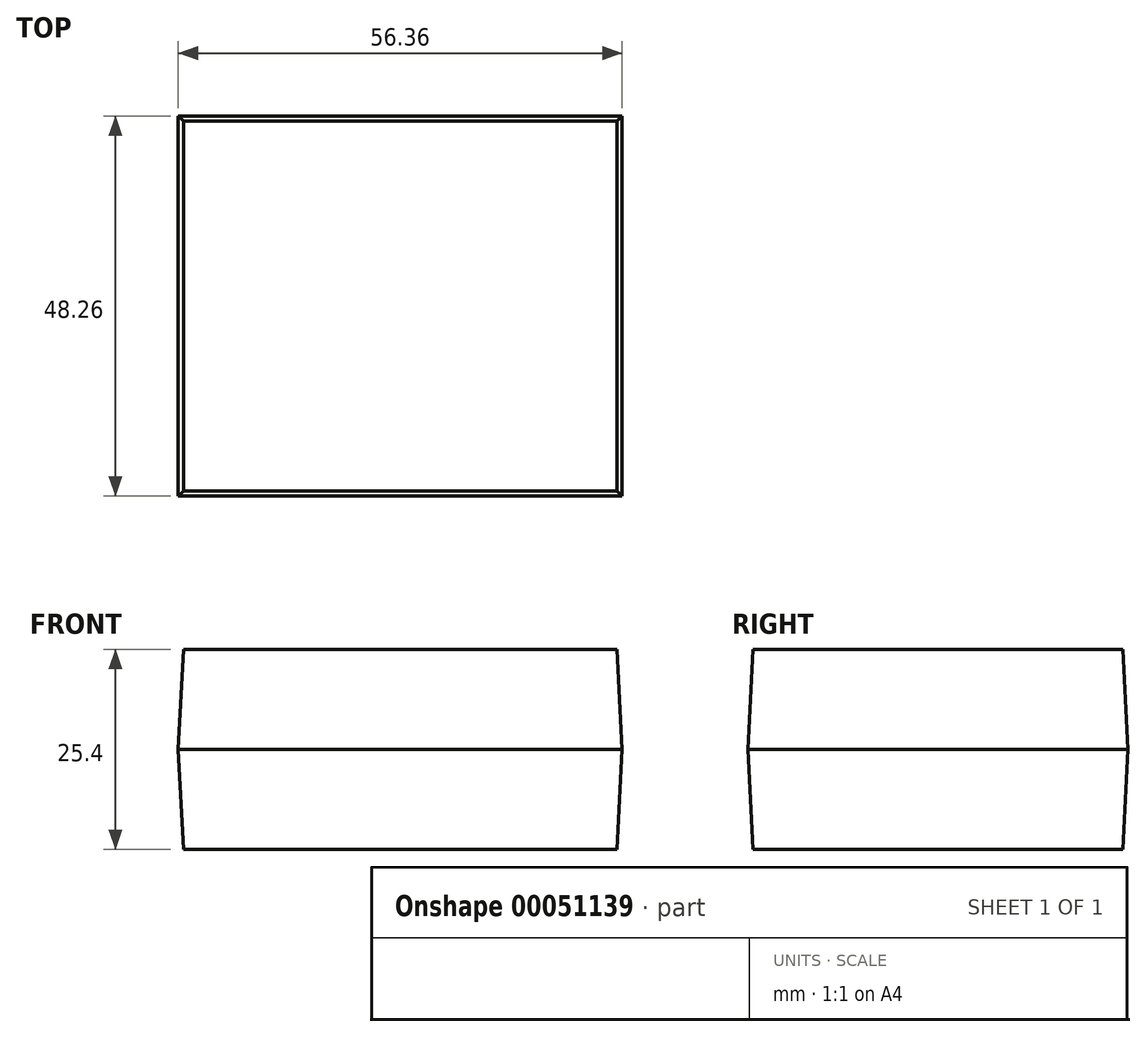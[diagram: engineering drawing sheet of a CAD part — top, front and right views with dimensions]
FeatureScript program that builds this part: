
annotation { "Feature Type Name" : "Feature", "Feature Type Description" : "" }
export const myFeature = defineFeature(function(context is Context, id is Id, definition is map)
    precondition{}
    {
        {
            var Q0;
            Q0=qCreatedBy(makeId("Top.planeOp"),FACE);
            var sketch = newSketch(context, id + "F0", { "sketchPlane" : qUnion([Q0])});
            skLineSegment(sketch, "E0.rect.bottom", {"start": v(28.18, -24.13) * mm, "end": v(-28.18, -24.13) * mm});
            skLineSegment(sketch, "E0.rect.top", {"start": v(28.18, 24.13) * mm, "end": v(-28.18, 24.13) * mm});
            skLineSegment(sketch, "E0.rect.left", {"start": v(28.18, -24.13) * mm, "end": v(28.18, 24.13) * mm});
            skLineSegment(sketch, "E0.rect.right", {"start": v(-28.18, -24.13) * mm, "end": v(-28.18, 24.13) * mm});
            skPoint(sketch, "E0.rect.middle", {"position": v(0, 0) * mm});
            skSolve(sketch);
        }
        {
            var Q0;
            Q0 = qSketchRegion(id + "F0", true);
            extrude(context, id + "F1", {"entities" : qUnion([Q0]), "endBound" : BoundingType.SYMMETRIC, "depth" : 25.4 * mm, "hasDraft" : true, "draftAngle" : 3 * degree, "draftPullDirection" : true});
        }
    });
